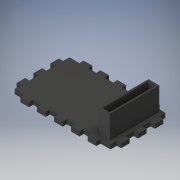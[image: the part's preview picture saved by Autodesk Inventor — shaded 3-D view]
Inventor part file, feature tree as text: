
AUTODESK INVENTOR PART (.ipt)
format: ipt  version: 2019 (Build 230136000, 136)  size: 219,648 bytes
history: native  units: mm
features: extrude x3, sketch x3
ambient origin geometry x8: Origin, YZ Plane, XZ Plane, XY Plane, X Axis, Y Axis, Z Axis, Center Point
bodies: Solid1 (feature_tree)
feature tree (6):
  extrude  "Extrusion1"  Depth=60.0mm
  extrude  "Extrusion2"  Depth=44.0mm
  extrude  "Extrusion3"  Depth=9.0mm
  sketch  "Sketch1"  dims[d0=99.0mm d1=60.0mm]
  sketch  "Sketch2"  dims[d2=7.0mm d3=44.0mm]
  sketch  "Sketch3"  dims[d4=8.0mm d5=9.0mm d6=4.0mm d7=0.0mm d8=1.5mm d9=22.0mm d10=0.0mm d11=4.0mm d12=8.0mm d13=4.0mm d14=8.0mm d15=8.0mm d16=4.0mm d17=8.0mm d18=8.0mm d19=8.0mm d20=22.0mm d21=0.0mm]
